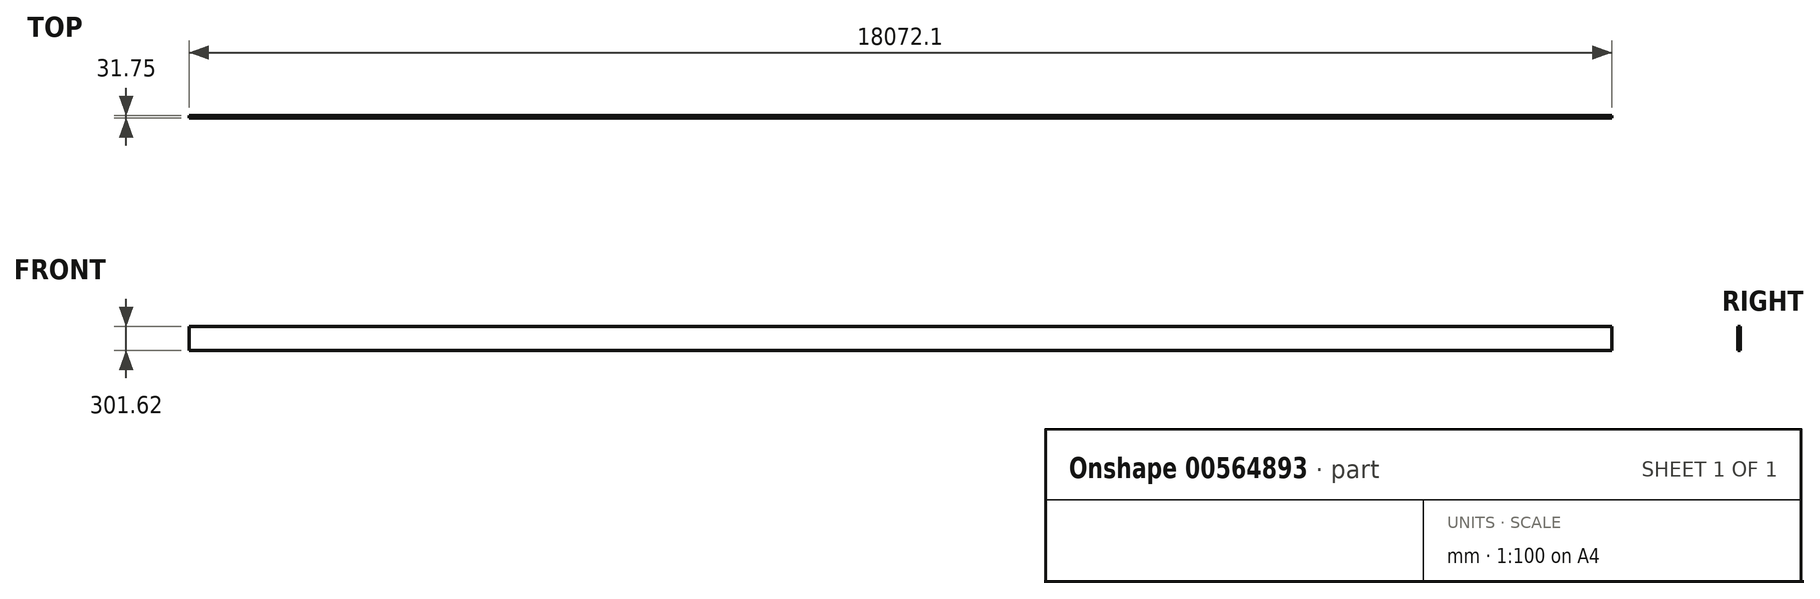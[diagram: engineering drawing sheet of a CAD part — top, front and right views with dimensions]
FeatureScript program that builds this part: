
annotation { "Feature Type Name" : "Feature", "Feature Type Description" : "" }
export const myFeature = defineFeature(function(context is Context, id is Id, definition is map)
    precondition{}
    {
        {
            var Q0;
            Q0=qCreatedBy(makeId("Right.planeOp"),FACE);
            var sketch = newSketch(context, id + "F0", { "sketchPlane" : qUnion([Q0])});
            skLineSegment(sketch, "E0.bottom", {"start": v(0, 0) * mm, "end": v(31.75, 0) * mm});
            skLineSegment(sketch, "E0.top", {"start": v(0, 301.62) * mm, "end": v(31.75, 301.62) * mm});
            skLineSegment(sketch, "E0.left", {"start": v(0, 0) * mm, "end": v(0, 301.62) * mm});
            skLineSegment(sketch, "E0.right", {"start": v(31.75, 0) * mm, "end": v(31.75, 301.63) * mm});
            skSolve(sketch);
        }
        {
            var Q0;
            Q0=qSketchRegion(id+"F0",true);
            extrude(context, id + "F1", {"entities" : qUnion([Q0]), "depth" : 18072.1 * mm, "offsetDistance" : 25.4 * mm});
        }
    });
